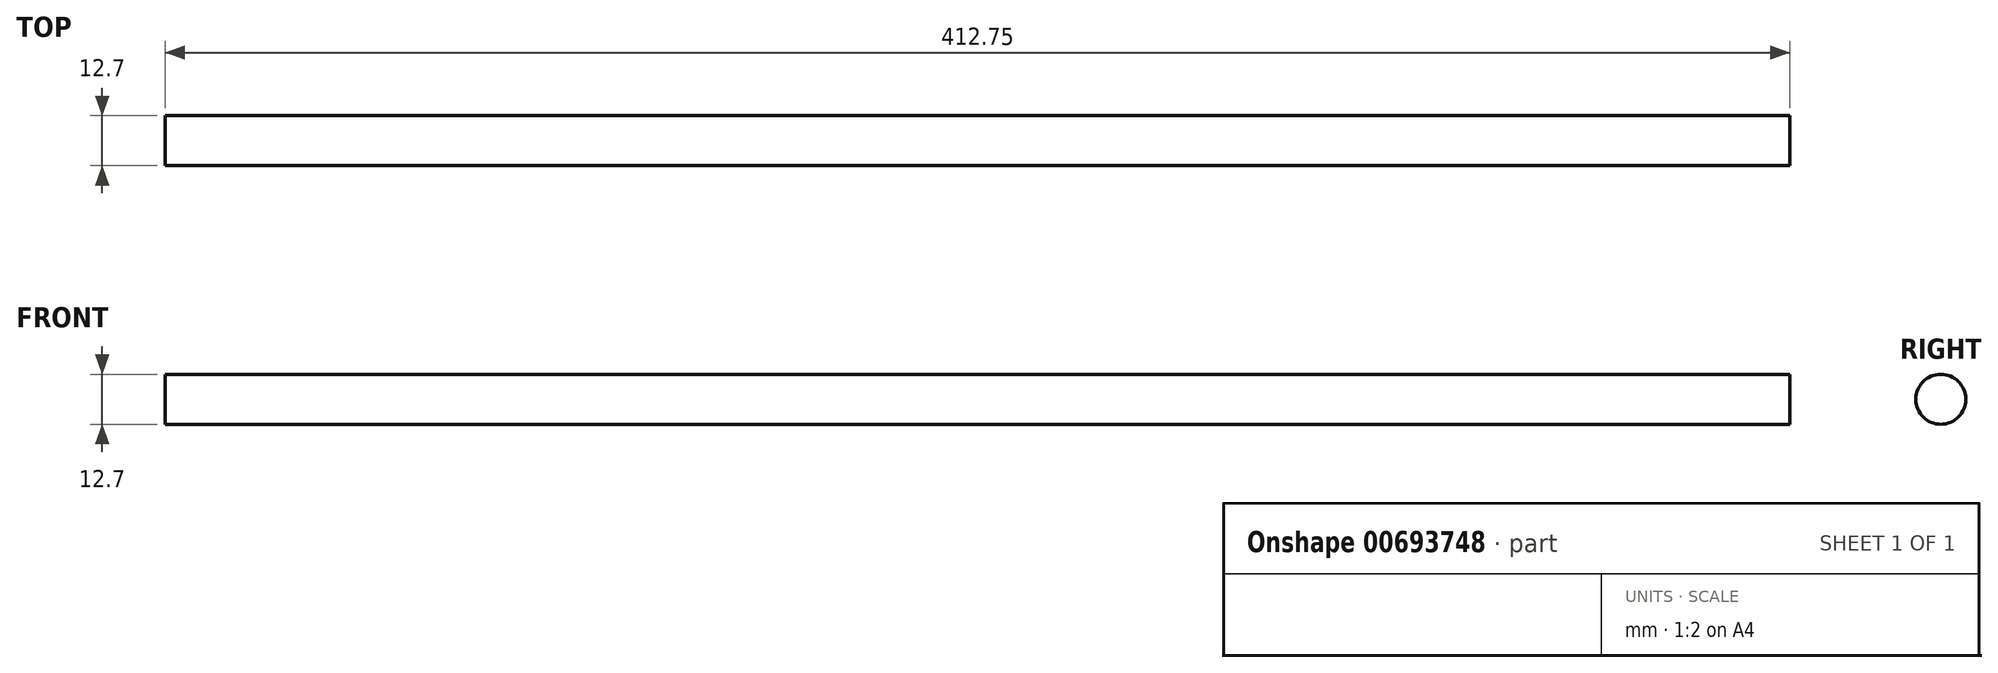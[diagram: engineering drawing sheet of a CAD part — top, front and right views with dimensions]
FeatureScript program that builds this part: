
annotation { "Feature Type Name" : "Feature", "Feature Type Description" : "" }
export const myFeature = defineFeature(function(context is Context, id is Id, definition is map)
    precondition{}
    {
        {
            var Q0;
            Q0=qCreatedBy(makeId("Right.planeOp"),FACE);
            var sketch = newSketch(context, id + "F0", { "sketchPlane" : qUnion([Q0])});
            skCircle(sketch, "E0", {"center": v(0, 0) * mm, "radius": 6.35 * mm});
            skSolve(sketch);
        }
        {
            var Q0;
            Q0=makeQuery(id+"F0.imprint","IMPRINT",FACE,{"disambiguationData":[TD([[makeQuery(id+"F0.imprint","IMPRINT",EDGE,{"derivedFrom":sQuery(id+"F0.wireOp",EDGE,"E0")}),1.0]])]});
            extrude(context, id + "F1", {"entities" : qUnion([Q0]), "depth" : 412.75 * mm, "offsetDistance" : 25.4 * mm});
        }
    });
